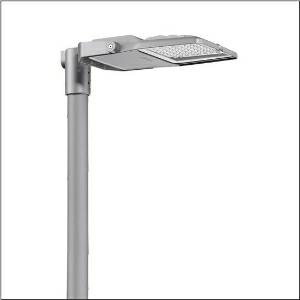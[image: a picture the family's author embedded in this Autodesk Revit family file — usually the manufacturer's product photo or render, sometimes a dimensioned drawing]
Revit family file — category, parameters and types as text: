
# Revit family: floodlight_fl_21_iq_mini___pl33t_5xa7771b4f3a_1cb2
name_source: partatom
category: Lighting Fixtures
units: mm (PartAtom-declared; Revit-internal decimal feet)

## family parameters
Cut with Voids When Loaded = No
Host = Face
Light Source = No
Part Type = Normal
Room Calculation Point = No
Round Connector Dimension = Use Diameter
Shared = No

## types (1)
- --- (1 x LED, 6420 lm, 45.5 W, 4000K)
    Apparent Load = 46 VA
    CIE Flux Codes = 26 75 99 100 100
    Color Rendering = 70
    Color Temperature = 4000K
    Default Elevation = 1800 mm
    Description = Floodlight FL 21 iQ mini, floodlight, primary light control with lens, of PMMA, primary optical cover: protective disc, of toughened safety glass, transparent, light distribution: PL33T, light emission: direct distribution, installation type: surface-mounted, lamps: LED, High Power LED, rated values: 6.420lm | 45,5W | 141,1lm/W (begin service life); end service life: 6.420lm | 48W; at 50% lumin. flux: 3.210lm | 21,5W | 149,3lm/W, colour temperature: 4000K, colour rendering: CRI > 70, light colour: 740, light setting 1 begin service life: 100% | 6.420lm | 45,5W | 141,1lm/W | 4.000K, light setting 1 end service life: 48W, further light settings possible, control: Auto-Match, Temp-Guard, Lumen-Switch, Night-Set, Smart-Wire, Light-Fading, Desk-Remote (wireless, voltage-free reading and setting of iQ features in the workshop via application-optimized NFC function/RFID function), optimised constant luminous flux control (CLO 2.0), pre-setting: linear dimming characteristic, with terminal, 6-pole, mains connection: 220..240V, AC, 50/60Hz, luminaire housing, of diecast aluminium, powder-coated, SITECO metallic grey (DB 702S), corrosivity category C5 mid according to DIN EN ISO 12944suitable for swimming poolschlorine-resistant, sealing non-destructively replaceable, please order mast flange separately, mast bracket, of steel, galvanised, powder-coated, SITECO metallic grey (DB 702S), protection rating (complete): IP66, insulation class (complete): insulation class II (safety insulation), certification: CE, ENEC, VDE, protection symbol: D, impact resistance: IK08, permissible operating ambient temperature: -40..+40°C, permissible operating ambient temperature for outdoor applications: -40..+50°C, standard: DIN EN 12944, LABS conformity tested according to VDMA 24364:2018-05, packaging unit: 1 piece

Light Distribution: PL33T
    Height = 70 mm
    Lamp = 1 x LED
    Lamp Light Flux = 6420 lm
    Lamp Power = 45.5 W
    Lamp count = 1
    Length = 485 mm
    Luminous efficacy = 141 lm/W
    Manufacturer = Siteco
    ModVariant = No
    Model = 5XA7771B4F3A
    Number of Poles = 1
    OnlyDefault = Yes
    Power Factor = 1
    Product Name = Floodlight FL 21 iQ mini | PL33T
    Product group = floodlight | pylon annexe
    ProductGroupID = 6201
    Protection Class = Protection class II
    Protection Degree = IP 66
    RLX_Detail_Level = 1
    RLX_Emergency_Light_Flux = 0 lm
    RLX_Emergency_Type = 0
    RLX_Emergency_Type_DB = No
    RlxData = <blob elided: 101317 chars, md5=fc54cc68>
    Socket = socket
    Standby Power = 0 W
    System Light Flux = 6420 lm
    System Power = 46 W
    Type Comments = factory setting: luminous flux: 100 % | dim-lin: 254 | 463 mA
    Type Image = l_1007125.jpg
    URL = http://relux.com
    VarID = @adj_149671
    Voltage = 0 V
    Weight = 0.00 kg
    Width = 337 mm

## geometry (parser evidence)
native form markers: Blend x4, Sweep x12
no freeform markers — native parametric forms only
